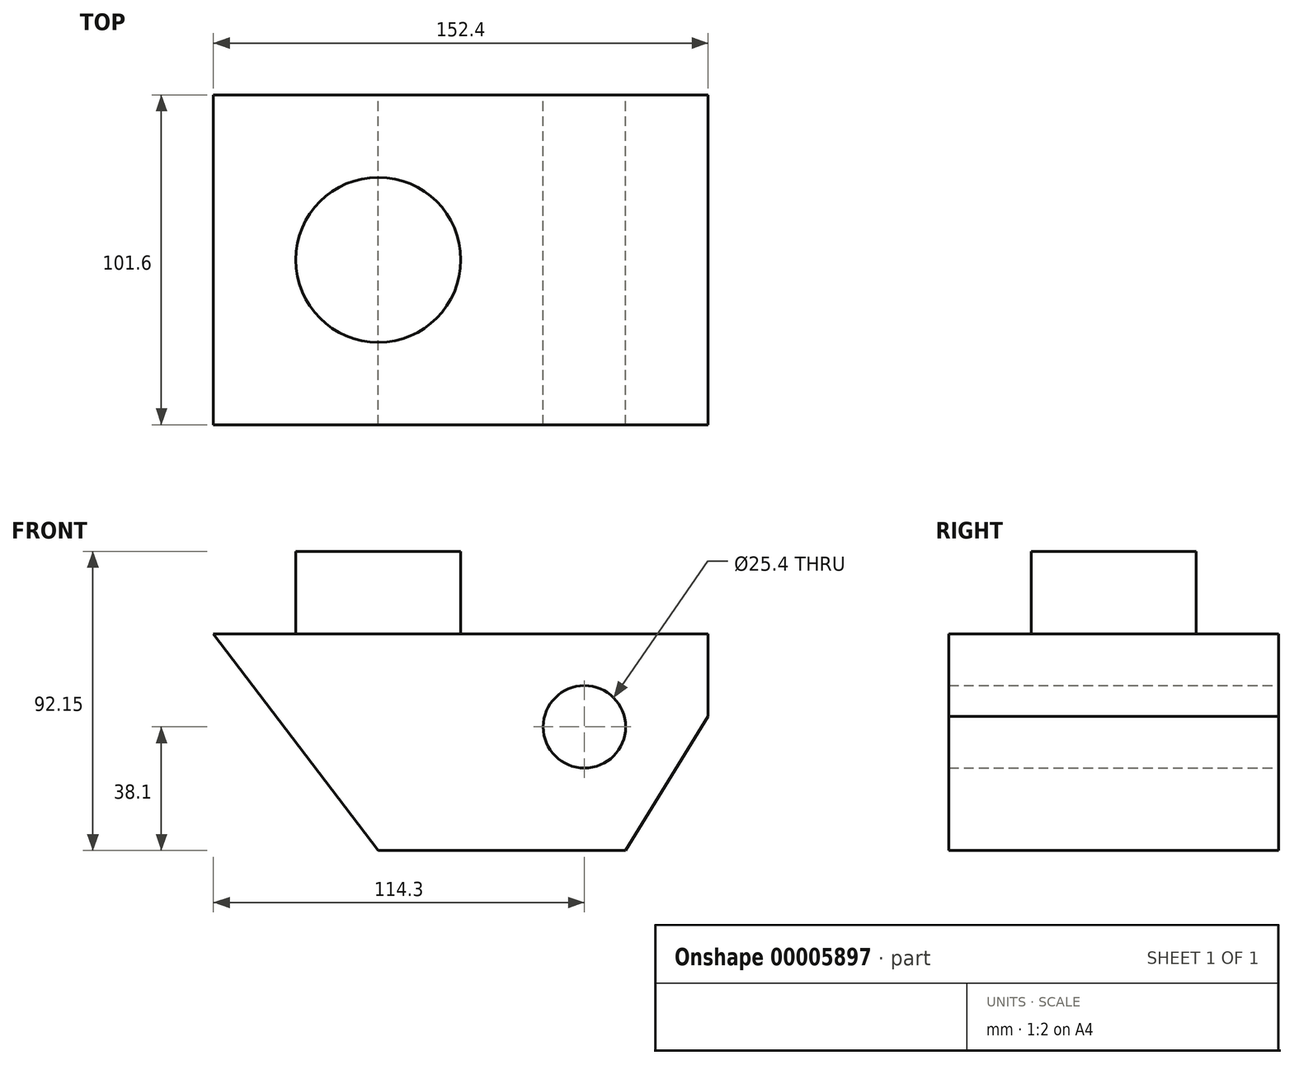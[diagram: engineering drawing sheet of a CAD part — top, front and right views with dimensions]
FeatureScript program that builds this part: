
annotation { "Feature Type Name" : "Feature", "Feature Type Description" : "" }
export const myFeature = defineFeature(function(context is Context, id is Id, definition is map)
    precondition{}
    {
        {
            var Q0;
            Q0=qCreatedBy(makeId("Front.planeOp"),FACE);
            var sketch = newSketch(context, id + "F0", { "sketchPlane" : qUnion([Q0])});
            skLineSegment(sketch, "E0", {"start": v(0, 0) * mm, "end": v(152.4, 0) * mm});
            skLineSegment(sketch, "E1", {"start": v(152.4, 0) * mm, "end": v(152.4, -25.4) * mm});
            skLineSegment(sketch, "E2", {"start": v(50.8, -66.75) * mm, "end": v(0, 0) * mm});
            skLineSegment(sketch, "E3", {"start": v(152.4, -25.4) * mm, "end": v(152.4, -66.75) * mm});
            skLineSegment(sketch, "E4", {"start": v(152.4, -66.75) * mm, "end": v(127, -66.75) * mm});
            skLineSegment(sketch, "E5", {"start": v(127, -66.75) * mm, "end": v(152.4, -25.4) * mm});
            skLineSegment(sketch, "E6", {"start": v(127, -66.75) * mm, "end": v(114.3, -66.75) * mm});
            skLineSegment(sketch, "E7", {"start": v(114.3, -66.75) * mm, "end": v(114.3, -28.65) * mm});
            skLineSegment(sketch, "E8", {"start": v(114.3, -66.75) * mm, "end": v(127, -66.75) * mm});
            skLineSegment(sketch, "E9", {"start": v(127, -66.75) * mm, "end": v(50.8, -66.75) * mm});
            skCircle(sketch, "E10", {"center": v(114.3, -28.65) * mm, "radius": 12.7 * mm});
            skSolve(sketch);
        }
        {
            var Q0;
            Q0=makeQuery(id+"F0.imprint","IMPRINT",FACE,{"disambiguationData":[TD([[makeQuery(id+"F0.imprint","IMPRINT",EDGE,{"derivedFrom":sQuery(id+"F0.wireOp",EDGE,"E0")}),-1.0]])]});
            extrude(context, id + "F1", {"entities" : qUnion([Q0]), "depth" : 101.6 * mm});
        }
        {
            var Q0;
            Q0=makeQuery(id+"F1.opExtrude","SWEPT_FACE",FACE,{"disambiguationData":[OSD([sQuery(id+"F0.wireOp",EDGE,"E0")])]});
            var sketch = newSketch(context, id + "F2", { "sketchPlane" : qUnion([Q0])});
            skLineSegment(sketch, "E11", {"start": v(0, -50.8) * mm, "end": v(50.8, -50.8) * mm});
            skCircle(sketch, "E12", {"center": v(50.8, -50.8) * mm, "radius": 25.4 * mm});
            skSolve(sketch);
        }
        {
            var Q0;
            {var subQ0=sQuery(id+"F2.wireOp",EDGE,"E12");Q0=makeQuery(id+"F2.imprint","IMPRINT",FACE,{"disambiguationData":[TD([[makeQuery(id+"F2.imprint","IMPRINT",EDGE,{"derivedFrom":subQ0}),1.0]])]});}
            extrude(context, id + "F3", {"entities" : qUnion([Q0]), "operationType" : NewBodyOperationType.ADD, "depth" : 25.4 * mm});
        }
    });
